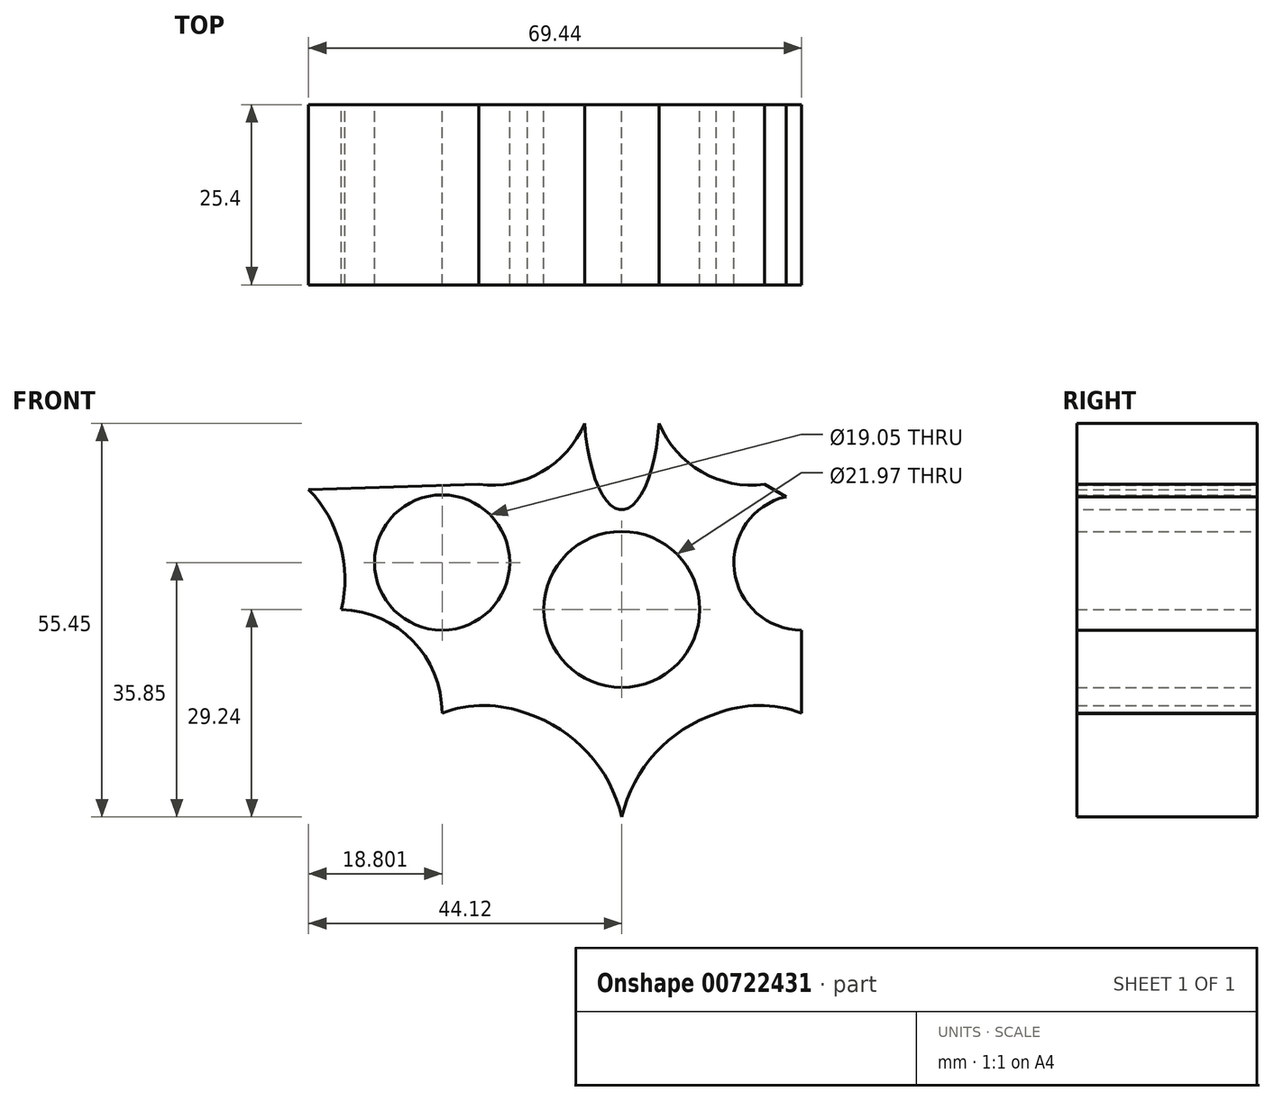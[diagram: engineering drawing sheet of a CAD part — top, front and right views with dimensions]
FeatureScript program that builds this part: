
annotation { "Feature Type Name" : "Feature", "Feature Type Description" : "" }
export const myFeature = defineFeature(function(context is Context, id is Id, definition is map)
    precondition{}
    {
        {
            var Q0;
            Q0=qCreatedBy(makeId("Front.planeOp"),FACE);
            var sketch = newSketch(context, id + "F0", { "sketchPlane" : qUnion([Q0])});
            skCircle(sketch, "E0.cCircle", {"center": v(0, 0) * mm, "radius": 25.32 * mm, "construction": true});
            skLineSegment(sketch, "E0.0", {"start": v(0, 29.24) * mm, "end": v(25.32, 14.62) * mm});
            skLineSegment(sketch, "E0.1", {"start": v(25.32, 14.62) * mm, "end": v(25.32, -14.62) * mm});
            skLineSegment(sketch, "E0.2", {"start": v(25.32, -14.62) * mm, "end": v(0, -29.24) * mm});
            skLineSegment(sketch, "E0.3", {"start": v(0, -29.24) * mm, "end": v(-25.32, -14.62) * mm});
            skLineSegment(sketch, "E0.4", {"start": v(-25.32, -14.62) * mm, "end": v(-25.32, 14.62) * mm});
            skLineSegment(sketch, "E0.5", {"start": v(-25.32, 14.62) * mm, "end": v(0, 29.24) * mm});
            skPoint(sketch, "E0.0.midPoint", {"position": v(12.66, 21.93) * mm});
            skEllipse(sketch, "E1", {"center": v(0, 29.24) * mm, "majorRadius": 15.22 * mm, "minorRadius": 5.35 * mm, "majorAxis": v(0, 1)});
            skCircle(sketch, "E2", {"center": v(0, 0) * mm, "radius": 10.99 * mm});
            skCircle(sketch, "E3", {"center": v(-18.36, 31.71) * mm, "radius": 14.22 * mm});
            skPoint(sketch, "E3.first.point", {"position": v(-5.25, 26.2) * mm});
            skPoint(sketch, "E3.second.point", {"position": v(-32.46, 33.53) * mm});
            skPoint(sketch, "E3.third.point", {"position": v(-24.66, 44.46) * mm});
            skCircle(sketch, "E4.MirrorC", {"center": v(18.36, 31.71) * mm, "radius": 14.22 * mm});
            skArc(sketch, "E5", {"start": v(13.32, -14.69) * mm, "mid": v(4.76, -20.22) * mm, "end": v(0, -29.24) * mm});
            skArc(sketch, "E6", {"start": v(25.32, -14.62) * mm, "mid": v(19.31, -13.55) * mm, "end": v(13.32, -14.69) * mm});
            skArc(sketch, "E7.MirrorCS", {"start": v(-25.32, -14.62) * mm, "mid": v(-19.31, -13.55) * mm, "end": v(-13.32, -14.69) * mm});
            skArc(sketch, "E8.MirrorCS", {"start": v(-13.32, -14.69) * mm, "mid": v(-4.76, -20.22) * mm, "end": v(0, -29.24) * mm});
            skArc(sketch, "E9", {"start": v(-25.32, -14.62) * mm, "mid": v(-29.45, -4.44) * mm, "end": v(-39.5, 0) * mm});
            skArc(sketch, "E10.MirrorCS", {"start": v(25.32, -14.62) * mm, "mid": v(29.45, -4.44) * mm, "end": v(39.5, 0) * mm});
            skArc(sketch, "E11", {"start": v(-39.5, 0) * mm, "mid": v(-39.66, 9.04) * mm, "end": v(-44.12, 16.9) * mm});
            skArc(sketch, "E12.MirrorCS", {"start": v(39.5, 0) * mm, "mid": v(39.66, 9.04) * mm, "end": v(44.12, 16.9) * mm});
            skLineSegment(sketch, "E13", {"start": v(-44.12, 16.9) * mm, "end": v(-20.15, 17.6) * mm});
            skLineSegment(sketch, "E14.MirrorCS", {"start": v(44.12, 16.9) * mm, "end": v(20.15, 17.6) * mm});
            skCircle(sketch, "E15", {"center": v(-25.32, 6.61) * mm, "radius": 9.53 * mm});
            skCircle(sketch, "E16.MirrorC", {"center": v(25.32, 6.61) * mm, "radius": 9.53 * mm});
            skSolve(sketch);
        }
        {
            var Q0;
            {var subQ0=sQuery(id+"F0.wireOp",EDGE,"E10.MirrorCS");Q0=makeQuery(id+"F0.imprint","IMPRINT",FACE,{"disambiguationData":[TD([[makeQuery(id+"F0.imprint","IMPRINT",EDGE,{"derivedFrom":subQ0}),1.0]])]});}
            var Q1;
            {var subQ0=sQuery(id+"F0.wireOp",EDGE,"E9");Q1=makeQuery(id+"F0.imprint","IMPRINT",FACE,{"disambiguationData":[TD([[makeQuery(id+"F0.imprint","IMPRINT",EDGE,{"derivedFrom":subQ0}),-1.0]])]});}
            var Q2;
            Q2=makeQuery(id+"F0.imprint","IMPRINT",FACE,{"disambiguationData":[TD([[makeQuery(id+"F0.imprint","IMPRINT",EDGE,{"derivedFrom":sQuery(id+"F0.wireOp",EDGE,"E2")}),-1.0]])]});
            extrude(context, id + "F1", {"entities" : qUnion([Q0, Q1, Q2]), "depth" : 25.4 * mm, "offsetDistance" : 25.4 * mm});
        }
    });
